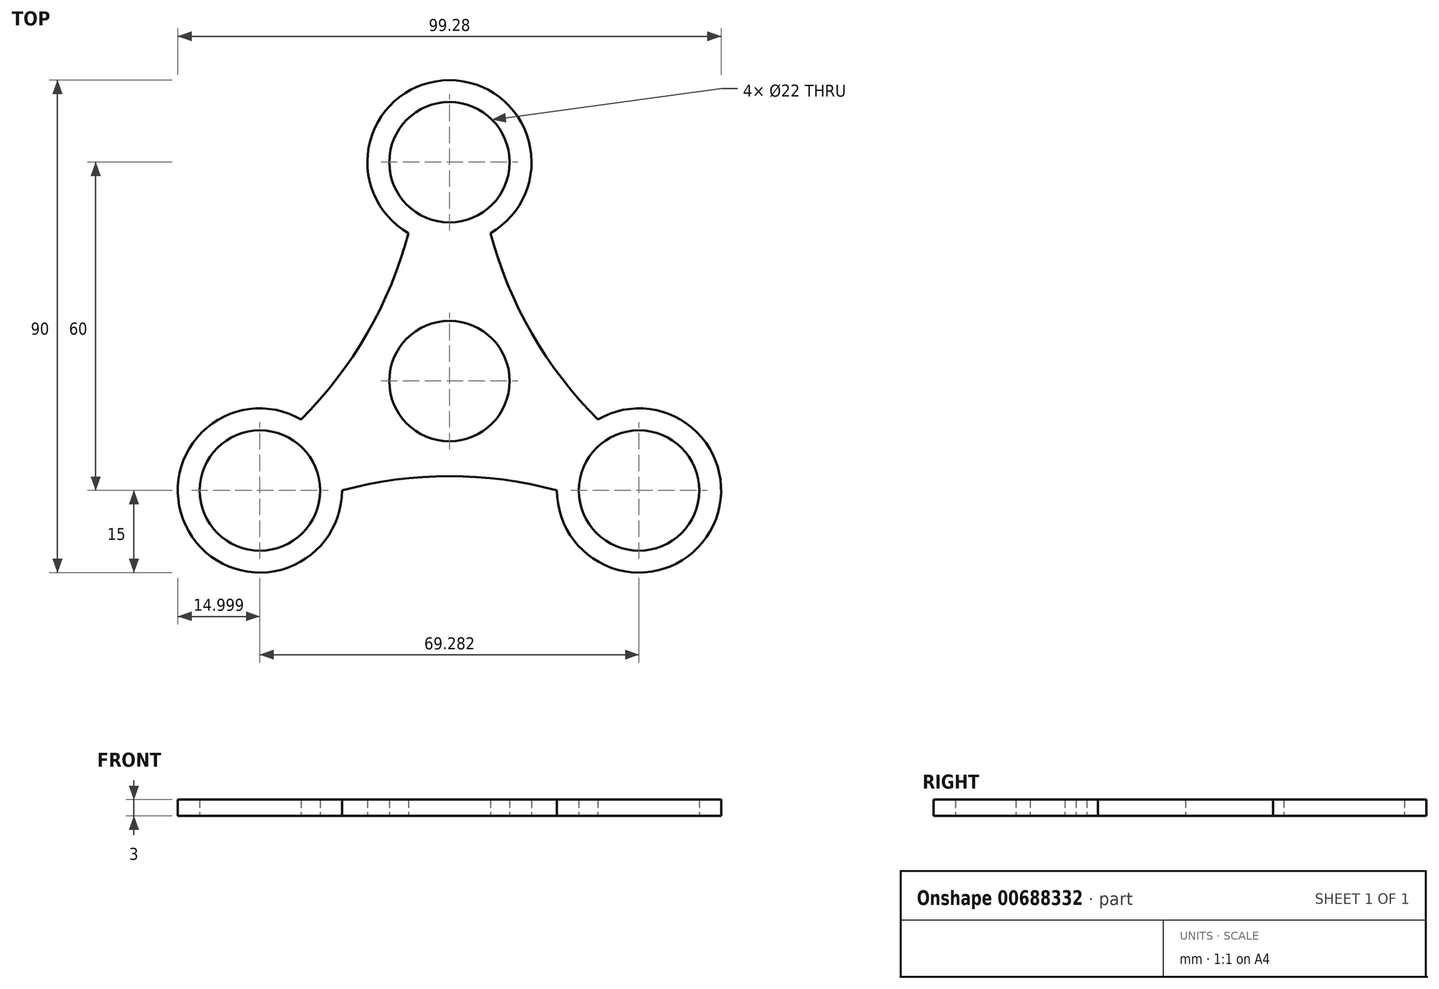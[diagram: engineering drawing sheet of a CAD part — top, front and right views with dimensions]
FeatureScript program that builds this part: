
annotation { "Feature Type Name" : "Feature", "Feature Type Description" : "" }
export const myFeature = defineFeature(function(context is Context, id is Id, definition is map)
    precondition{}
    {
        {
            var Q0;
            Q0=qCreatedBy(makeId("Top.planeOp"),FACE);
            var sketch = newSketch(context, id + "F0", { "sketchPlane" : qUnion([Q0])});
            skCircle(sketch, "E0", {"center": v(0, 0) * mm, "radius": 11 * mm});
            skPoint(sketch, "E1.0.midPoint", {"position": v(0, -20) * mm});
            skCircle(sketch, "E2", {"center": v(0, 40) * mm, "radius": 11 * mm});
            skArc(sketch, "E3", {"start": v(7.5, 27) * mm, "mid": v(0, 55) * mm, "end": v(-7.5, 27) * mm});
            skCircle(sketch, "E4", {"center": v(-34.64, -20) * mm, "radius": 11 * mm});
            skArc(sketch, "E5", {"start": v(-27.14, -7) * mm, "mid": v(-47.63, -27.5) * mm, "end": v(-19.64, -20) * mm});
            skCircle(sketch, "E6", {"center": v(34.64, -20) * mm, "radius": 11 * mm});
            skArc(sketch, "E7", {"start": v(19.64, -20) * mm, "mid": v(47.63, -27.5) * mm, "end": v(27.14, -7) * mm});
            skArc(sketch, "E8", {"start": v(-27.14, -7) * mm, "mid": v(-15.05, 8.7) * mm, "end": v(-7.5, 27) * mm});
            skArc(sketch, "E9", {"start": v(19.64, -20) * mm, "mid": v(0, -17.38) * mm, "end": v(-19.64, -20) * mm});
            skArc(sketch, "E10", {"start": v(7.5, 27) * mm, "mid": v(15.05, 8.7) * mm, "end": v(27.14, -7) * mm});
            skSolve(sketch);
        }
        {
            var Q0;
            Q0 = qSketchRegion(id + "F0", true);
            extrude(context, id + "F1", {"entities" : qUnion([Q0]), "depth" : 3 * mm, "offsetDistance" : 25 * mm});
        }
    });
